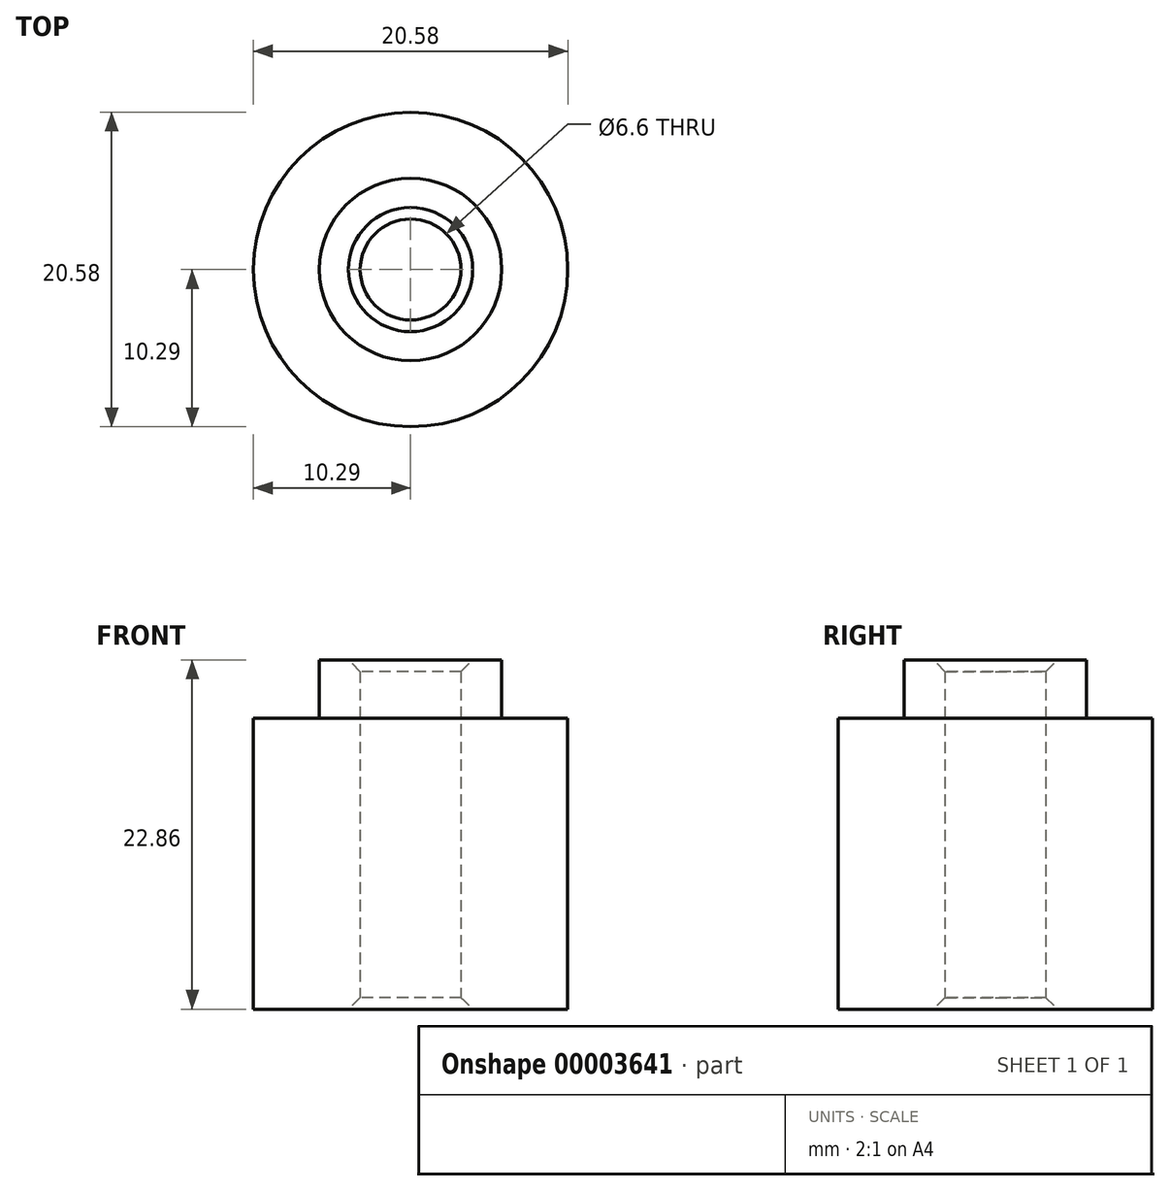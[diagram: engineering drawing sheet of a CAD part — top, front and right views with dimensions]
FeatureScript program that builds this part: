
annotation { "Feature Type Name" : "Feature", "Feature Type Description" : "" }
export const myFeature = defineFeature(function(context is Context, id is Id, definition is map)
    precondition{}
    {
        {
            var Q0;
            Q0=qCreatedBy(makeId("Top.planeOp"),FACE);
            var sketch = newSketch(context, id + "F0", { "sketchPlane" : qUnion([Q0])});
            skCircle(sketch, "E0", {"center": v(0, 0) * mm, "radius": 10.29 * mm});
            skCircle(sketch, "E1", {"center": v(0, 0) * mm, "radius": 3.3 * mm});
            skSolve(sketch);
        }
        {
            var Q0;
            Q0=qSketchRegion(id+"F0",true);
            extrude(context, id + "F1", {"entities" : qUnion([Q0]), "depth" : 19.05 * mm});
        }
        {
            var Q0;
            Q0=makeQuery(id+"F1.opExtrude","CAP_FACE",FACE,{"disambiguationData":[OSD([sQuery(id+"F0.wireOp",EDGE,"E0"),sQuery(id+"F0.wireOp",EDGE,"E1")])],"isStart":true});
            var sketch = newSketch(context, id + "F2", { "sketchPlane" : qUnion([Q0])});
            skCircle(sketch, "E2", {"center": v(0, 0) * mm, "radius": 9.27 * mm});
            skCircle(sketch, "E3.0", {"center": v(0, 0) * mm, "radius": 10.29 * mm});
            skSolve(sketch);
        }
        {
            var Q0;
            Q0=makeQuery(id+"F1.opExtrude","CAP_FACE",FACE,{"disambiguationData":[OSD([sQuery(id+"F0.wireOp",EDGE,"E0"),sQuery(id+"F0.wireOp",EDGE,"E1")])],"isStart":false});
            var sketch = newSketch(context, id + "F3", { "sketchPlane" : qUnion([Q0])});
            skCircle(sketch, "E4", {"center": v(0, 0) * mm, "radius": 5.97 * mm});
            skCircle(sketch, "E5.0", {"center": v(0, 0) * mm, "radius": 3.3 * mm});
            skSolve(sketch);
        }
        {
            var Q0;
            Q0=qSketchRegion(id+"F3",true);
            extrude(context, id + "F4", {"entities" : qUnion([Q0]), "operationType" : NewBodyOperationType.ADD, "depth" : 3.8 * mm});
        }
        {
            var Q0;
            Q0=makeQuery(id+"F4.opExtrude","CAP_EDGE",EDGE,{"disambiguationData":[OSD([sQuery(id+"F3.wireOp",EDGE,"E5.0")])],"isStart":false});
            var Q1;
            Q1=makeQuery(id+"F1.opExtrude","CAP_EDGE",EDGE,{"disambiguationData":[OSD([sQuery(id+"F0.wireOp",EDGE,"E1")])],"isStart":true});
            chamfer(context, id + "F5", {"entities" : qUnion([Q0, Q1]), "width" : 0.76 * mm, "tangentPropagation" : true});
        }
    });
